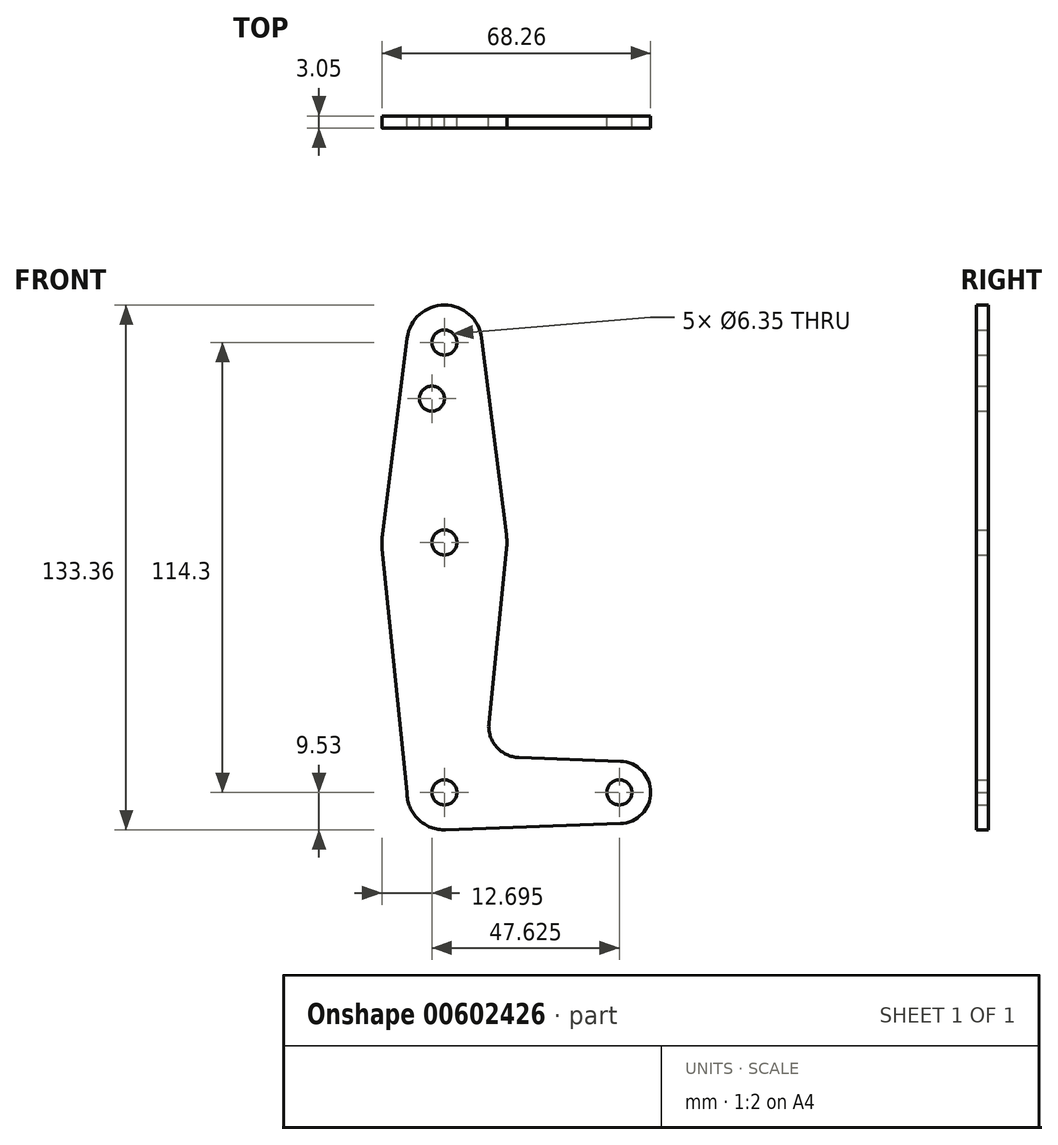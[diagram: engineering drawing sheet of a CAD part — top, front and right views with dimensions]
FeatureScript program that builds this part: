
annotation { "Feature Type Name" : "Feature", "Feature Type Description" : "" }
export const myFeature = defineFeature(function(context is Context, id is Id, definition is map)
    precondition{}
    {
        {
            var Q0;
            Q0=qCreatedBy(makeId("Front.planeOp"),FACE);
            var sketch = newSketch(context, id + "F0", { "sketchPlane" : qUnion([Q0])});
            skLineSegment(sketch, "E0", {"start": v(0, 0) * mm, "end": v(0, 114.3) * mm});
            skLineSegment(sketch, "E1", {"start": v(0, 0) * mm, "end": v(44.45, 0) * mm});
            skCircle(sketch, "E2", {"center": v(0, 0) * mm, "radius": 9.52 * mm});
            skCircle(sketch, "E3", {"center": v(44.45, 0) * mm, "radius": 7.94 * mm});
            skCircle(sketch, "E4", {"center": v(0, 114.3) * mm, "radius": 9.53 * mm});
            skCircle(sketch, "E5", {"center": v(0, 63.5) * mm, "radius": 15.88 * mm});
            skLineSegment(sketch, "E6", {"start": v(-9.52, 0) * mm, "end": v(-15.8, 61.9) * mm});
            skLineSegment(sketch, "E7", {"start": v(-9.45, 115.5) * mm, "end": v(-15.75, 65.48) * mm});
            skLineSegment(sketch, "E8", {"start": v(44.73, -7.93) * mm, "end": v(0.34, -9.52) * mm});
            skLineSegment(sketch, "E9.MirrorCS", {"start": v(9.45, 115.5) * mm, "end": v(15.75, 65.48) * mm});
            skLineSegment(sketch, "E10.MirrorCS", {"start": v(11.3, 17.6) * mm, "end": v(15.8, 61.9) * mm});
            skLineSegment(sketch, "E11.MirrorCS", {"start": v(44.73, 7.93) * mm, "end": v(18.93, 8.85) * mm});
            skCircle(sketch, "E12", {"center": v(0, 114.3) * mm, "radius": 3.18 * mm});
            skCircle(sketch, "E13", {"center": v(0, 63.5) * mm, "radius": 3.18 * mm});
            skCircle(sketch, "E14", {"center": v(0, 0) * mm, "radius": 3.18 * mm});
            skCircle(sketch, "E15", {"center": v(-3.18, 100.03) * mm, "radius": 3.18 * mm});
            skCircle(sketch, "E16", {"center": v(44.45, 0) * mm, "radius": 3.18 * mm});
            skPoint(sketch, "E17.newPointA", {"position": v(0.34, 9.52) * mm});
            skPoint(sketch, "E17.newPointB", {"position": v(9.52, 0) * mm});
            skArc(sketch, "E17.filletArc", {"start": v(11.3, 17.6) * mm, "mid": v(13.22, 11.57) * mm, "end": v(18.93, 8.85) * mm});
            skSolve(sketch);
        }
        {
            var Q0;
            Q0=makeQuery(id+"F0.imprint","IMPRINT",FACE,{"disambiguationData":[TD([[makeQuery(id+"F0.imprint","IMPRINT",EDGE,{"derivedFrom":sQuery(id+"F0.wireOp",EDGE,"E12")}),-1.0]])]});
            var Q1;
            {var subQ0=sQuery(id+"F0.wireOp",EDGE,"E9.MirrorCS");Q1=makeQuery(id+"F0.imprint","IMPRINT",FACE,{"disambiguationData":[TD([[makeQuery(id+"F0.imprint","IMPRINT",EDGE,{"derivedFrom":subQ0}),-1.0]])]});}
            var Q2;
            {var subQ0=sQuery(id+"F0.wireOp",EDGE,"E7");Q2=makeQuery(id+"F0.imprint","IMPRINT",FACE,{"disambiguationData":[TD([[makeQuery(id+"F0.imprint","IMPRINT",EDGE,{"derivedFrom":subQ0}),1.0]])]});}
            var Q3;
            {var subQ0=sQuery(id+"F0.wireOp",EDGE,"E5");var subQ2=sQuery(id+"F0.wireOp",EDGE,"E0");var subQ8=makeQuery(id+"F0.imprint","INTERSECT",VERTEX,{"disambiguationData":[OD(0.0)],"derivedFrom":[subQ2,subQ0]});Q3=makeQuery(id+"F0.imprint","IMPRINT",FACE,{"disambiguationData":[TD([[makeQuery(id+"F0.imprint","IMPRINT",EDGE,{"disambiguationData":[TD([[subQ8,-1.0]])],"derivedFrom":subQ2}),1.0]])]});}
            var Q4;
            {var subQ0=sQuery(id+"F0.wireOp",EDGE,"E5");var subQ2=sQuery(id+"F0.wireOp",EDGE,"E0");var subQ5=makeQuery(id+"F0.imprint","INTERSECT",VERTEX,{"disambiguationData":[OD(0.0)],"derivedFrom":[subQ2,subQ0]});Q4=makeQuery(id+"F0.imprint","IMPRINT",FACE,{"disambiguationData":[TD([[makeQuery(id+"F0.imprint","IMPRINT",EDGE,{"disambiguationData":[TD([[subQ5,-1.0]])],"derivedFrom":subQ2}),-1.0]])]});}
            var Q5;
            {var subQ10=sQuery(id+"F0.wireOp",EDGE,"E10.MirrorCS");Q5=makeQuery(id+"F0.imprint","IMPRINT",FACE,{"disambiguationData":[TD([[makeQuery(id+"F0.imprint","IMPRINT",EDGE,{"derivedFrom":subQ10}),1.0]])]});}
            var Q6;
            {var subQ5=sQuery(id+"F0.wireOp",EDGE,"E6");Q6=makeQuery(id+"F0.imprint","IMPRINT",FACE,{"disambiguationData":[TD([[makeQuery(id+"F0.imprint","IMPRINT",EDGE,{"derivedFrom":subQ5}),-1.0]])]});}
            var Q7;
            {var subQ5=sQuery(id+"F0.wireOp",EDGE,"E8");Q7=makeQuery(id+"F0.imprint","IMPRINT",FACE,{"disambiguationData":[TD([[makeQuery(id+"F0.imprint","IMPRINT",EDGE,{"derivedFrom":subQ5}),-1.0]])]});}
            var Q8;
            {var subQ3=sQuery(id+"F0.wireOp",EDGE,"E0");var subQ5=sQuery(id+"F0.wireOp",EDGE,"E14");var subQ6=makeQuery(id+"F0.imprint","INTERSECT",VERTEX,{"derivedFrom":[subQ3,subQ5]});Q8=makeQuery(id+"F0.imprint","IMPRINT",FACE,{"disambiguationData":[TD([[makeQuery(id+"F0.imprint","IMPRINT",EDGE,{"disambiguationData":[TD([[subQ6,-1.0]])],"derivedFrom":subQ3}),1.0]])]});}
            var Q9;
            {var subQ0=sQuery(id+"F0.wireOp",EDGE,"E14");var subQ1=sQuery(id+"F0.wireOp",EDGE,"E0");var subQ2=makeQuery(id+"F0.imprint","INTERSECT",VERTEX,{"derivedFrom":[subQ1,subQ0]});Q9=makeQuery(id+"F0.imprint","IMPRINT",FACE,{"disambiguationData":[TD([[makeQuery(id+"F0.imprint","IMPRINT",EDGE,{"disambiguationData":[TD([[subQ2,-1.0]])],"derivedFrom":subQ1}),-1.0]])]});}
            var Q10;
            Q10=makeQuery(id+"F0.imprint","IMPRINT",FACE,{"disambiguationData":[TD([[makeQuery(id+"F0.imprint","IMPRINT",EDGE,{"derivedFrom":sQuery(id+"F0.wireOp",EDGE,"E16")}),-1.0]])]});
            extrude(context, id + "F1", {"entities" : qUnion([Q0, Q1, Q2, Q3, Q4, Q5, Q6, Q7, Q8, Q9, Q10]), "depth" : 3.05 * mm, "offsetDistance" : 25.4 * mm});
        }
    });
